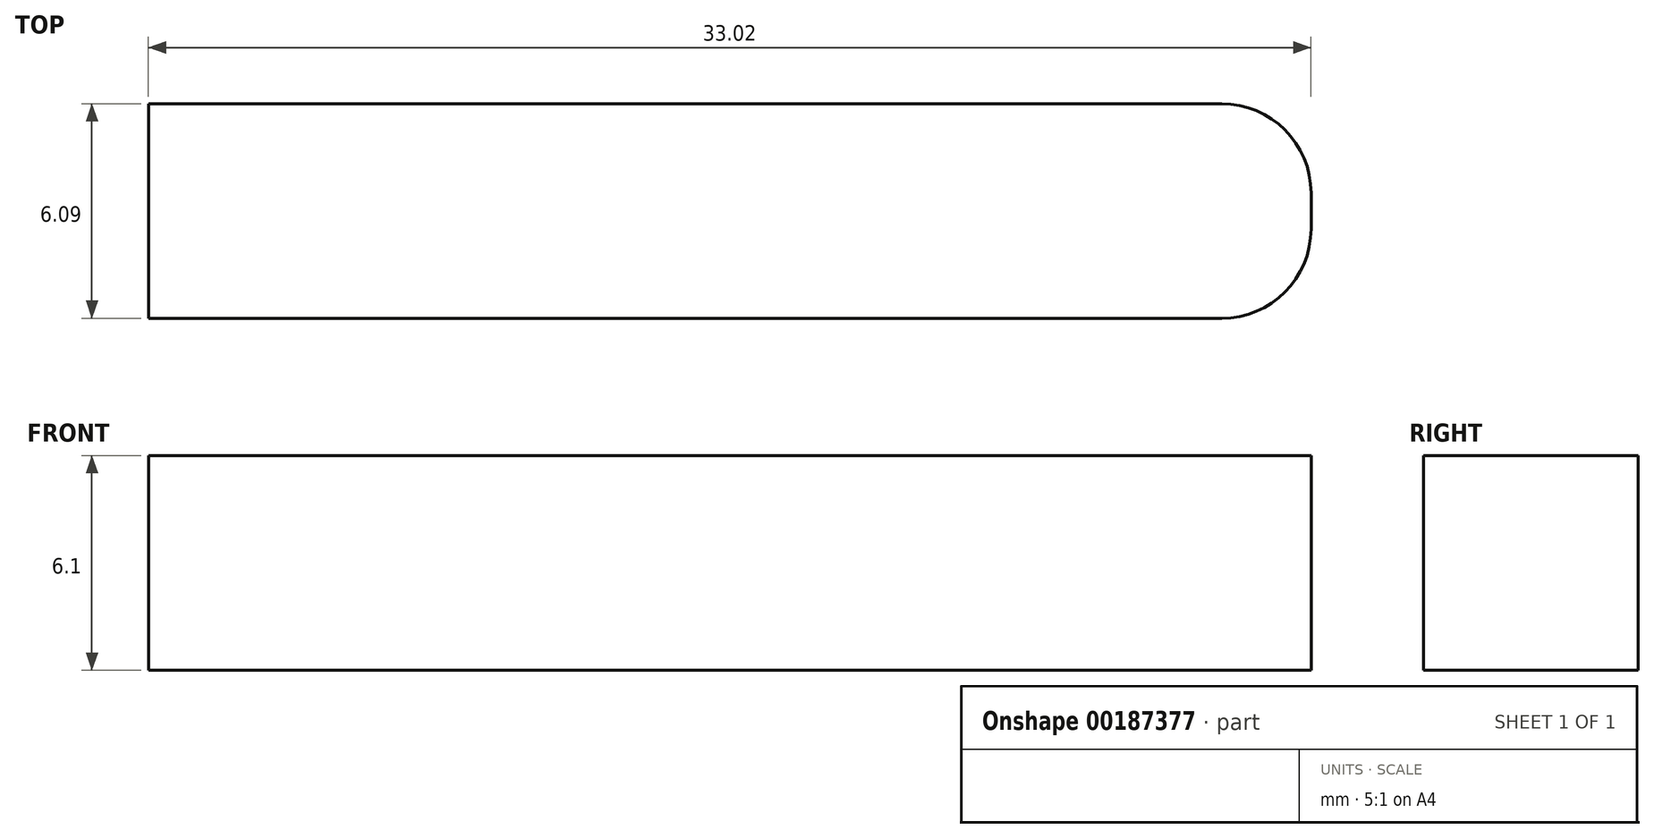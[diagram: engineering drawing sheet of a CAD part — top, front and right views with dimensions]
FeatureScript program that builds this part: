
annotation { "Feature Type Name" : "Feature", "Feature Type Description" : "" }
export const myFeature = defineFeature(function(context is Context, id is Id, definition is map)
    precondition{}
    {
        {
            var Q0;
            Q0=qCreatedBy(makeId("Top.planeOp"),FACE);
            var sketch = newSketch(context, id + "F0", { "sketchPlane" : qUnion([Q0])});
            skLineSegment(sketch, "E0.bottom", {"start": v(-5.79, -6.47) * mm, "end": v(27.23, -6.47) * mm});
            skLineSegment(sketch, "E0.top", {"start": v(-5.79, -0.38) * mm, "end": v(27.23, -0.38) * mm});
            skLineSegment(sketch, "E0.left", {"start": v(-5.79, -6.47) * mm, "end": v(-5.79, -0.38) * mm});
            skLineSegment(sketch, "E0.right", {"start": v(27.23, -6.47) * mm, "end": v(27.23, -0.38) * mm});
            skSolve(sketch);
        }
        {
            var Q0;
            Q0=makeQuery(id+"F0.imprint","IMPRINT",FACE,{"disambiguationData":[TD([[makeQuery(id+"F0.imprint","IMPRINT",EDGE,{"derivedFrom":sQuery(id+"F0.wireOp",EDGE,"E0.bottom")}),1.0]])]});
            extrude(context, id + "F1", {"entities" : qUnion([Q0]), "depth" : 6.1 * mm});
        }
        {
            var Q0;
            Q0=makeQuery(id+"F1.opExtrude","SWEPT_EDGE",EDGE,{"disambiguationData":[OSD([sQuery(id+"F0.wireOp",EDGE,"E0.bottom"),sQuery(id+"F0.wireOp",EDGE,"E0.right")])]});
            var Q1;
            Q1=makeQuery(id+"F1.opExtrude","SWEPT_EDGE",EDGE,{"disambiguationData":[OSD([sQuery(id+"F0.wireOp",EDGE,"E0.top"),sQuery(id+"F0.wireOp",EDGE,"E0.right")])]});
            fillet(context, id + "F2", {"entities" : qUnion([Q0, Q1]), "radius" : 2.54 * mm, "tangentPropagation" : true, "allowEdgeOverflow" : false});
        }
    });
